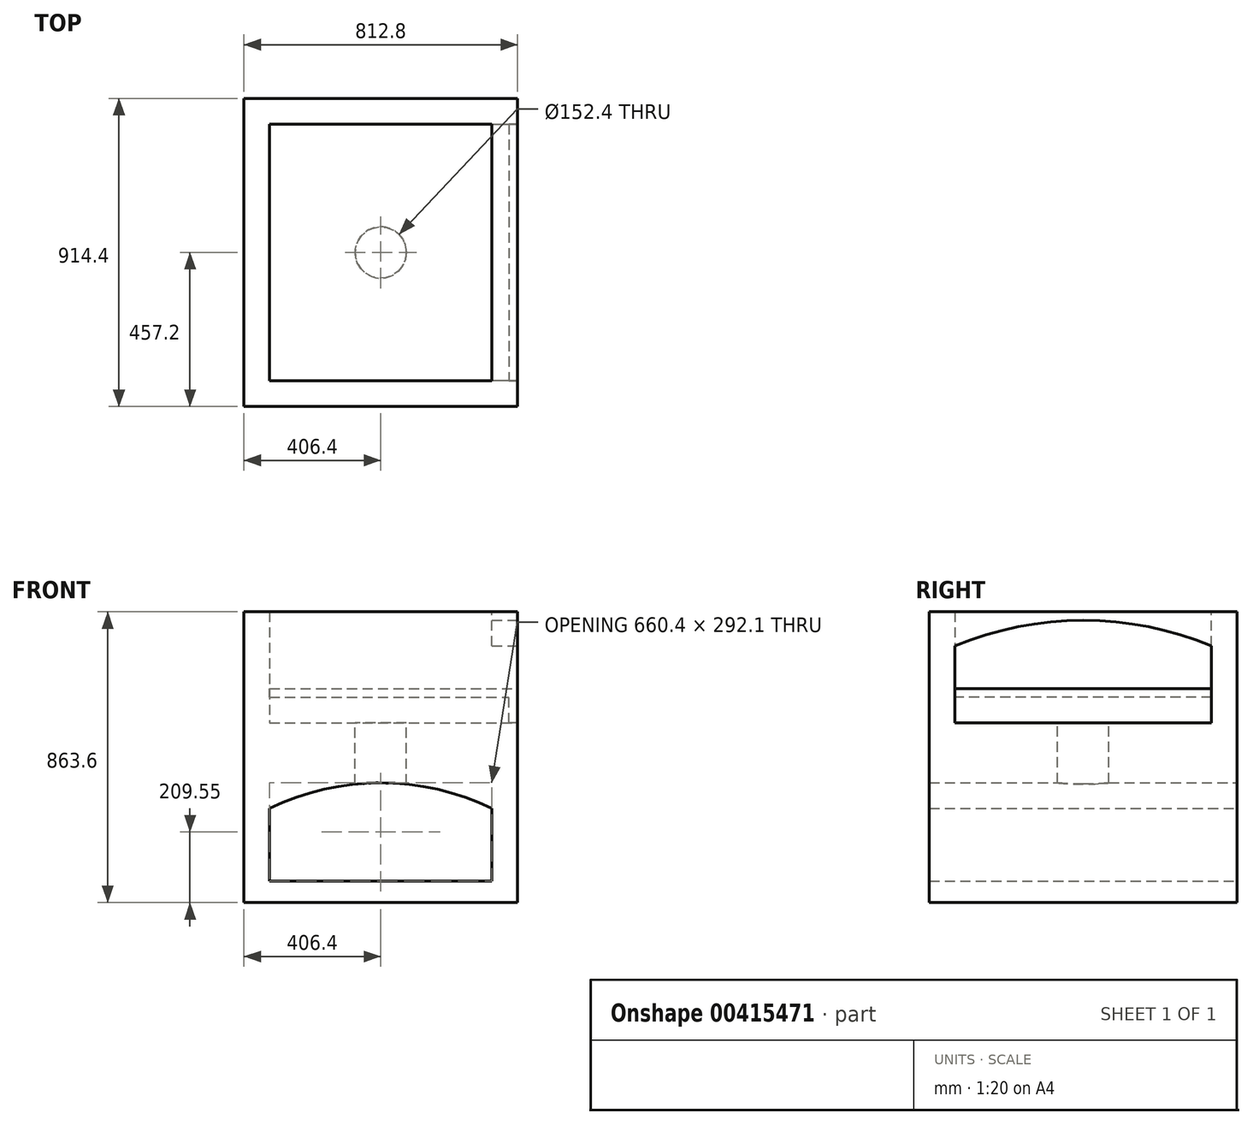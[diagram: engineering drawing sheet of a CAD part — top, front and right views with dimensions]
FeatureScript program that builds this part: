
annotation { "Feature Type Name" : "Feature", "Feature Type Description" : "" }
export const myFeature = defineFeature(function(context is Context, id is Id, definition is map)
    precondition{}
    {
        {
            var Q0;
            Q0=qCreatedBy(makeId("Top.planeOp"),FACE);
            var sketch = newSketch(context, id + "F0", { "sketchPlane" : qUnion([Q0])});
            skLineSegment(sketch, "E0.bottom", {"start": v(406.4, -457.2) * mm, "end": v(-406.4, -457.2) * mm});
            skLineSegment(sketch, "E0.top", {"start": v(406.4, 457.2) * mm, "end": v(-406.4, 457.2) * mm});
            skLineSegment(sketch, "E0.left", {"start": v(406.4, -457.2) * mm, "end": v(406.4, 457.2) * mm});
            skLineSegment(sketch, "E0.right", {"start": v(-406.4, -457.2) * mm, "end": v(-406.4, 457.2) * mm});
            skPoint(sketch, "E0.middle", {"position": v(0, 0) * mm});
            skSolve(sketch);
        }
        {
            var Q0;
            Q0=makeQuery(id+"F0.imprint","IMPRINT",FACE,{"disambiguationData":[TD([[makeQuery(id+"F0.imprint","IMPRINT",EDGE,{"derivedFrom":sQuery(id+"F0.wireOp",EDGE,"E0.bottom")}),-1.0]])]});
            extrude(context, id + "F1", {"entities" : qUnion([Q0]), "depth" : 863.6 * mm});
        }
        {
            var Q0;
            Q0=makeQuery(id+"F1.opExtrude","SWEPT_FACE",FACE,{"disambiguationData":[OSD([sQuery(id+"F0.wireOp",EDGE,"E0.left")])]});
            var sketch = newSketch(context, id + "F2", { "sketchPlane" : qUnion([Q0])});
            skLineSegment(sketch, "E1.top", {"start": v(-381, 533.4) * mm, "end": v(381, 533.4) * mm});
            skPoint(sketch, "E2", {"position": v(-457.2, 533.4) * mm});
            skPoint(sketch, "E3", {"position": v(-381, 762) * mm});
            skPoint(sketch, "E4", {"position": v(381, 762) * mm});
            skPoint(sketch, "E5", {"position": v(0, 838.2) * mm});
            skArc(sketch, "E6", {"start": v(381, 762) * mm, "mid": v(0, 838.2) * mm, "end": v(-381, 762) * mm});
            skLineSegment(sketch, "E7", {"start": v(-381, 762) * mm, "end": v(-381, 533.4) * mm});
            skLineSegment(sketch, "E8", {"start": v(381, 762) * mm, "end": v(381, 533.4) * mm});
            skSolve(sketch);
        }
        {
            var Q0;
            Q0=makeQuery(id+"F2.imprint","IMPRINT",FACE,{"disambiguationData":[TD([[makeQuery(id+"F2.imprint","IMPRINT",EDGE,{"derivedFrom":sQuery(id+"F2.wireOp",EDGE,"E1.top")}),1.0]])]});
            extrude(context, id + "F3", {"entities" : qUnion([Q0]), "operationType" : NewBodyOperationType.REMOVE, "oppositeDirection" : true, "depth" : 736.6 * mm});
        }
        {
            var Q0;
            Q0=makeQuery(id+"F1.opExtrude","CAP_FACE",FACE,{"disambiguationData":[OSD([sQuery(id+"F0.wireOp",EDGE,"E0.bottom"),sQuery(id+"F0.wireOp",EDGE,"E0.top"),sQuery(id+"F0.wireOp",EDGE,"E0.left"),sQuery(id+"F0.wireOp",EDGE,"E0.right")])],"isStart":false});
            var sketch = newSketch(context, id + "F4", { "sketchPlane" : qUnion([Q0])});
            skLineSegment(sketch, "E9.bottom", {"start": v(-330.2, 381) * mm, "end": v(330.2, 381) * mm});
            skLineSegment(sketch, "E9.top", {"start": v(-330.2, -381) * mm, "end": v(330.2, -381) * mm});
            skLineSegment(sketch, "E9.left", {"start": v(-330.2, 381) * mm, "end": v(-330.2, -381) * mm});
            skLineSegment(sketch, "E9.right", {"start": v(330.2, 381) * mm, "end": v(330.2, -381) * mm});
            skSolve(sketch);
        }
        {
            var Q0;
            Q0=makeQuery(id+"F4.imprint","IMPRINT",FACE,{"disambiguationData":[TD([[makeQuery(id+"F4.imprint","IMPRINT",EDGE,{"derivedFrom":sQuery(id+"F4.wireOp",EDGE,"E9.bottom")}),-1.0]])]});
            extrude(context, id + "F5", {"entities" : qUnion([Q0]), "operationType" : NewBodyOperationType.REMOVE, "endBound" : BoundingType.UP_TO_NEXT, "oppositeDirection" : true, "depth" : 25.4 * mm});
        }
        {
            var Q0;
            Q0=makeQuery(id+"F1.opExtrude","SWEPT_FACE",FACE,{"disambiguationData":[OSD([sQuery(id+"F0.wireOp",EDGE,"E0.top")])]});
            var sketch = newSketch(context, id + "F6", { "sketchPlane" : qUnion([Q0])});
            skPoint(sketch, "E10", {"position": v(-406.4, 431.8) * mm});
            skLineSegment(sketch, "E11", {"start": v(-406.4, 431.8) * mm, "end": v(406.4, 431.8) * mm});
            skPoint(sketch, "E12", {"position": v(0, 355.6) * mm});
            skPoint(sketch, "E12.positionSnap0", {"position": v(0, 431.8) * mm});
            skPoint(sketch, "E13", {"position": v(-330.2, 279.4) * mm});
            skPoint(sketch, "E14", {"position": v(-406.4, 279.4) * mm});
            skPoint(sketch, "E15", {"position": v(406.4, 279.4) * mm});
            skPoint(sketch, "E16", {"position": v(330.2, 279.4) * mm});
            skPoint(sketch, "E17", {"position": v(0, 63.5) * mm});
            skPoint(sketch, "E18", {"position": v(0, 0) * mm});
            skLineSegment(sketch, "E19.bottom", {"start": v(-330.2, 63.5) * mm, "end": v(330.2, 63.5) * mm});
            skLineSegment(sketch, "E19.top", {"start": v(-330.2, 355.6) * mm, "end": v(330.2, 355.6) * mm});
            skLineSegment(sketch, "E19.left", {"start": v(-330.2, 63.5) * mm, "end": v(-330.2, 355.6) * mm});
            skLineSegment(sketch, "E19.right", {"start": v(330.2, 63.5) * mm, "end": v(330.2, 355.6) * mm});
            skArc(sketch, "E20", {"start": v(330.2, 279.4) * mm, "mid": v(0, 355.6) * mm, "end": v(-330.2, 279.4) * mm});
            skSolve(sketch);
        }
        {
            var Q0;
            {var subQ5=sQuery(id+"F6.wireOp",EDGE,"E19.bottom");Q0=makeQuery(id+"F6.imprint","IMPRINT",FACE,{"disambiguationData":[TD([[makeQuery(id+"F6.imprint","IMPRINT",EDGE,{"derivedFrom":subQ5}),1.0]])]});}
            extrude(context, id + "F7", {"entities" : qUnion([Q0]), "operationType" : NewBodyOperationType.REMOVE, "endBound" : BoundingType.THROUGH_ALL, "oppositeDirection" : true, "depth" : 25.4 * mm});
        }
        {
            var Q0;
            Q0=makeQuery(id+"F3.boolean.opBoolean","COPY",FACE,{"derivedFrom":makeQuery(id+"F3.opExtrude","SWEPT_FACE",FACE,{"disambiguationData":[OSD([sQuery(id+"F2.wireOp",EDGE,"E1.top")])]})});
            var sketch = newSketch(context, id + "F8", { "sketchPlane" : qUnion([Q0])});
            skCircle(sketch, "E21", {"center": v(0, 0) * mm, "radius": 76.2 * mm});
            skSolve(sketch);
        }
        {
            var Q0;
            Q0=makeQuery(id+"F8.imprint","IMPRINT",FACE,{"disambiguationData":[TD([[makeQuery(id+"F8.imprint","IMPRINT",EDGE,{"derivedFrom":sQuery(id+"F8.wireOp",EDGE,"E21")}),1.0]])]});
            extrude(context, id + "F9", {"entities" : qUnion([Q0]), "operationType" : NewBodyOperationType.REMOVE, "endBound" : BoundingType.UP_TO_NEXT, "oppositeDirection" : true, "depth" : 25.4 * mm});
        }
        {
            var Q0;
            Q0=makeQuery(id+"F5.boolean.opBoolean","MERGE",FACE,{"derivedFrom":[makeQuery(id+"F3.boolean.opBoolean","COPY",FACE,{"derivedFrom":makeQuery(id+"F3.opExtrude","SWEPT_FACE",FACE,{"disambiguationData":[OSD([sQuery(id+"F2.wireOp",EDGE,"E7")])]})}),makeQuery(id+"F5.opExtrude","SWEPT_FACE",FACE,{"disambiguationData":[OSD([sQuery(id+"F4.wireOp",EDGE,"E9.top")])]})]});
            var sketch = newSketch(context, id + "F10", { "sketchPlane" : qUnion([Q0])});
            skLineSegment(sketch, "E22", {"start": v(-406.4, 609.6) * mm, "end": v(330.2, 609.6) * mm});
            skLineSegment(sketch, "E23", {"start": v(-406.4, 635) * mm, "end": v(330.2, 635) * mm});
            skLineSegment(sketch, "E24", {"start": v(-381, 609.6) * mm, "end": v(-381, 533.4) * mm});
            skSolve(sketch);
        }
        {
            var Q0;
            {var subQ0=sQuery(id+"F10.wireOp",EDGE,"E23");Q0=makeQuery(id+"F10.imprint","IMPRINT",FACE,{"disambiguationData":[TD([[makeQuery(id+"F10.imprint","IMPRINT",EDGE,{"derivedFrom":subQ0}),-1.0]])]});}
            var Q1;
            {var subQ4=sQuery(id+"F10.wireOp",EDGE,"E24");Q1=makeQuery(id+"F10.imprint","IMPRINT",FACE,{"disambiguationData":[TD([[makeQuery(id+"F10.imprint","IMPRINT",EDGE,{"derivedFrom":subQ4}),-1.0]])]});}
            extrude(context, id + "F11", {"entities" : qUnion([Q0, Q1]), "endBound" : BoundingType.UP_TO_NEXT, "depth" : 25.4 * mm});
        }
    });
